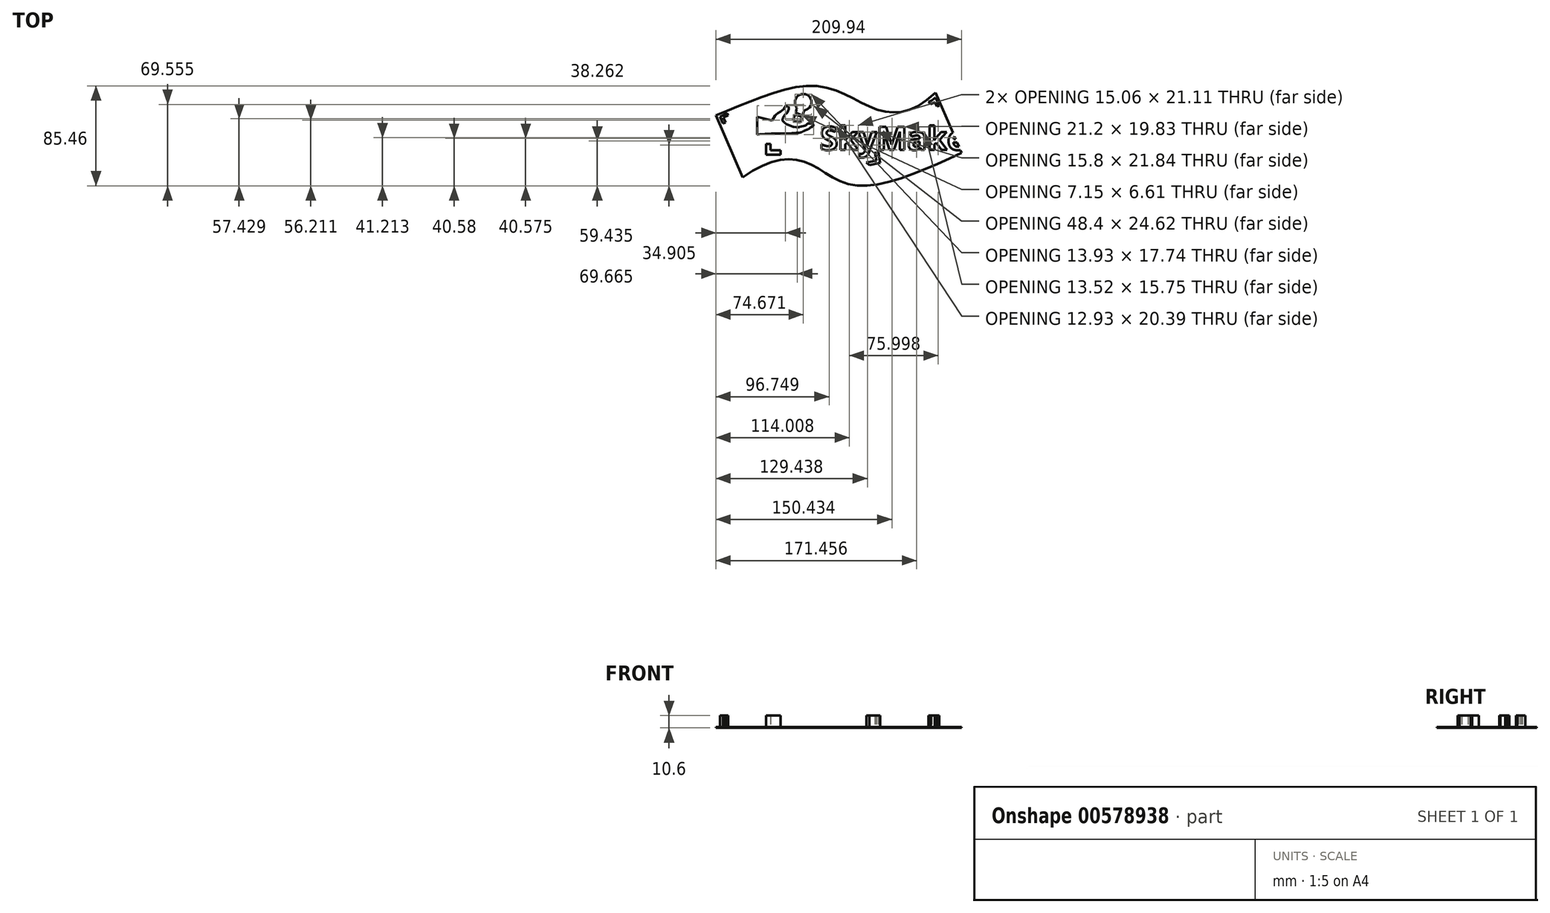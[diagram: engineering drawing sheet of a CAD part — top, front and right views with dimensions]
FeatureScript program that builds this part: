
annotation { "Feature Type Name" : "Feature", "Feature Type Description" : "" }
export const myFeature = defineFeature(function(context is Context, id is Id, definition is map)
    precondition{}
    {
        {
            var Q0;
            Q0=qCreatedBy(makeId("Top.planeOp"),FACE);
            var sketch = newSketch(context, id + "F0", { "sketchPlane" : qUnion([Q0])});
            skLineSegment(sketch, "E0.left", {"start": v(-41.02, -28.62) * mm, "end": v(-63.9, 24.41) * mm});
            skLineSegment(sketch, "E0.right", {"start": v(146.04, -7.8) * mm, "end": v(123.74, 43.89) * mm});
            skFitSpline(sketch, "E1", {"points": [v(-41.02, -28.62) * mm, v(12.17, -15.38) * mm, v(53.5, -35.29) * mm, v(146.04, -7.8) * mm], "startDerivative": vector(200.09, 142.74) * mm, "endDerivative": vector(235.03, 108.17) * mm});
            skFitSpline(sketch, "E2", {"points": [v(123.74, 43.89) * mm, v(75.61, 28.75) * mm, v(22.77, 49.35) * mm, v(-63.9, 24.41) * mm], "startDerivative": vector(-176.83, -170.43) * mm, "endDerivative": vector(-218, -84.69) * mm});
            skSolve(sketch);
        }
        {
            var Q0;
            Q0=qSketchRegion(id+"F0",true);
            extrude(context, id + "F1", {"entities" : qUnion([Q0]), "depth" : 0.6 * mm, "offsetDistance" : 25 * mm});
        }
        {
            var Q0;
            Q0=makeQuery(id+"F1.opExtrude","CAP_FACE",FACE,{"disambiguationData":[OSD([sQuery(id+"F0.wireOp",EDGE,"E0.left"),sQuery(id+"F0.wireOp",EDGE,"E0.right"),sQuery(id+"F0.wireOp",EDGE,"E1"),sQuery(id+"F0.wireOp",EDGE,"E2")])],"isStart":false});
            var sketch = newSketch(context, id + "F2", { "sketchPlane" : qUnion([Q0])});
            skLineSegment(sketch, "E3", {"start": v(-57.77, 17.46) * mm, "end": v(-60.47, 23.24) * mm});
            skLineSegment(sketch, "E4", {"start": v(-60.47, 23.24) * mm, "end": v(-54.23, 26.16) * mm});
            skLineSegment(sketch, "E5", {"start": v(-54.23, 26.16) * mm, "end": v(-53.41, 24.41) * mm});
            skLineSegment(sketch, "E6", {"start": v(-53.41, 24.41) * mm, "end": v(-57.6, 22.46) * mm});
            skLineSegment(sketch, "E7", {"start": v(-57.6, 22.46) * mm, "end": v(-55.72, 18.45) * mm});
            skLineSegment(sketch, "E8", {"start": v(-55.72, 18.45) * mm, "end": v(-57.77, 17.46) * mm});
            skLineSegment(sketch, "E9", {"start": v(120.7, 37.13) * mm, "end": v(123.74, 39.7) * mm});
            skLineSegment(sketch, "E10", {"start": v(123.74, 39.7) * mm, "end": v(126.87, 32.76) * mm});
            skLineSegment(sketch, "E11", {"start": v(126.87, 32.76) * mm, "end": v(124.93, 31.88) * mm});
            skLineSegment(sketch, "E12", {"start": v(124.93, 31.88) * mm, "end": v(123.23, 35.66) * mm});
            skLineSegment(sketch, "E13", {"start": v(123.23, 35.66) * mm, "end": v(119.62, 34.03) * mm});
            skLineSegment(sketch, "E14", {"start": v(119.62, 34.03) * mm, "end": v(117.61, 35.97) * mm});
            skLineSegment(sketch, "E15", {"start": v(117.61, 35.97) * mm, "end": v(120.7, 37.13) * mm});
            skLineSegment(sketch, "E16", {"start": v(67.21, -18.03) * mm, "end": v(76.47, -16.36) * mm});
            skLineSegment(sketch, "E17", {"start": v(76.47, -16.36) * mm, "end": v(74.78, -7.01) * mm});
            skLineSegment(sketch, "E18", {"start": v(74.78, -7.01) * mm, "end": v(71.93, -7.53) * mm});
            skLineSegment(sketch, "E19", {"start": v(71.93, -7.53) * mm, "end": v(73.18, -14.44) * mm});
            skLineSegment(sketch, "E20", {"start": v(73.18, -14.44) * mm, "end": v(64.63, -15.99) * mm});
            skLineSegment(sketch, "E21", {"start": v(64.63, -15.99) * mm, "end": v(67.21, -18.03) * mm});
            skLineSegment(sketch, "E22", {"start": v(-20.87, -2.86) * mm, "end": v(-20.87, -9.16) * mm});
            skLineSegment(sketch, "E23", {"start": v(-20.87, -9.16) * mm, "end": v(-8.52, -9.16) * mm});
            skLineSegment(sketch, "E24", {"start": v(-8.52, -9.16) * mm, "end": v(-8.52, -5.56) * mm});
            skLineSegment(sketch, "E25", {"start": v(-8.52, -5.56) * mm, "end": v(-17.27, -5.56) * mm});
            skLineSegment(sketch, "E26", {"start": v(-17.27, -5.56) * mm, "end": v(-17.27, 0) * mm});
            skLineSegment(sketch, "E27", {"start": v(-17.27, 0) * mm, "end": v(-20.87, 0) * mm});
            skLineSegment(sketch, "E28", {"start": v(-20.87, 0) * mm, "end": v(-20.87, -2.86) * mm});
            skSolve(sketch);
        }
        {
            var Q0;
            Q0 = qSketchRegion(id + "F2", true);
            extrude(context, id + "F3", {"entities" : qUnion([Q0]), "operationType" : NewBodyOperationType.ADD, "depth" : 10 * mm, "offsetDistance" : 25 * mm});
        }
        {
            var Q0;
            Q0=qCreatedBy(makeId("Top.planeOp"),FACE);
            var sketch = newSketch(context, id + "F4", { "sketchPlane" : qUnion([Q0])});
            skLineSegment(sketch, "E29", {"start": v(-28.66, 23.04) * mm, "end": v(-28.66, 8.04) * mm});
            skLineSegment(sketch, "E30", {"start": v(-28.66, 8.04) * mm, "end": v(-26.69, 8.18) * mm});
            skLineSegment(sketch, "E31", {"start": v(-26.69, 8.18) * mm, "end": v(-22.05, 8.48) * mm});
            skLineSegment(sketch, "E32", {"start": v(-22.05, 8.48) * mm, "end": v(-16.7, 8.77) * mm});
            skLineSegment(sketch, "E33", {"start": v(-16.7, 8.77) * mm, "end": v(-13.54, 8.9) * mm});
            skLineSegment(sketch, "E34", {"start": v(-13.54, 8.9) * mm, "end": v(-12.59, 8.9) * mm});
            skLineSegment(sketch, "E35", {"start": v(-12.59, 8.9) * mm, "end": v(-12.08, 8.9) * mm});
            skLineSegment(sketch, "E36", {"start": v(-12.08, 8.9) * mm, "end": v(-10.54, 8.86) * mm});
            skLineSegment(sketch, "E37", {"start": v(-10.54, 8.86) * mm, "end": v(-7.72, 8.8) * mm});
            skLineSegment(sketch, "E38", {"start": v(-7.72, 8.8) * mm, "end": v(-5.06, 8.76) * mm});
            skLineSegment(sketch, "E39", {"start": v(-5.06, 8.76) * mm, "end": v(-3.7, 8.74) * mm});
            skLineSegment(sketch, "E40", {"start": v(-3.7, 8.74) * mm, "end": v(-3.44, 8.75) * mm});
            skLineSegment(sketch, "E41", {"start": v(-3.44, 8.75) * mm, "end": v(-3.15, 8.76) * mm});
            skLineSegment(sketch, "E42", {"start": v(-3.15, 8.76) * mm, "end": v(-1.15, 8.92) * mm});
            skLineSegment(sketch, "E43", {"start": v(-1.15, 8.92) * mm, "end": v(0.81, 9.1) * mm});
            skLineSegment(sketch, "E44", {"start": v(0.81, 9.1) * mm, "end": v(1.1, 9.11) * mm});
            skLineSegment(sketch, "E45", {"start": v(1.1, 9.11) * mm, "end": v(1.39, 9.14) * mm});
            skLineSegment(sketch, "E46", {"start": v(1.39, 9.14) * mm, "end": v(2.76, 9.2) * mm});
            skLineSegment(sketch, "E47", {"start": v(2.76, 9.2) * mm, "end": v(4.3, 9.3) * mm});
            skLineSegment(sketch, "E48", {"start": v(4.3, 9.3) * mm, "end": v(4.68, 9.32) * mm});
            skLineSegment(sketch, "E49", {"start": v(4.68, 9.32) * mm, "end": v(5.17, 9.36) * mm});
            skLineSegment(sketch, "E50", {"start": v(5.17, 9.36) * mm, "end": v(7.1, 9.44) * mm});
            skLineSegment(sketch, "E51", {"start": v(7.1, 9.44) * mm, "end": v(8.6, 9.68) * mm});
            skLineSegment(sketch, "E52", {"start": v(8.6, 9.68) * mm, "end": v(8.88, 9.8) * mm});
            skLineSegment(sketch, "E53", {"start": v(8.88, 9.8) * mm, "end": v(9.07, 9.88) * mm});
            skLineSegment(sketch, "E54", {"start": v(9.07, 9.88) * mm, "end": v(10.04, 10.4) * mm});
            skLineSegment(sketch, "E55", {"start": v(10.04, 10.4) * mm, "end": v(11.2, 11.04) * mm});
            skLineSegment(sketch, "E56", {"start": v(11.2, 11.04) * mm, "end": v(11.5, 11.16) * mm});
            skLineSegment(sketch, "E57", {"start": v(11.5, 11.16) * mm, "end": v(11.9, 11.35) * mm});
            skLineSegment(sketch, "E58", {"start": v(11.9, 11.35) * mm, "end": v(13.49, 11.95) * mm});
            skLineSegment(sketch, "E59", {"start": v(13.49, 11.95) * mm, "end": v(14.57, 12.32) * mm});
            skLineSegment(sketch, "E60", {"start": v(14.57, 12.32) * mm, "end": v(14.73, 12.4) * mm});
            skLineSegment(sketch, "E61", {"start": v(14.73, 12.4) * mm, "end": v(14.89, 12.47) * mm});
            skLineSegment(sketch, "E62", {"start": v(14.89, 12.47) * mm, "end": v(15.73, 13.08) * mm});
            skLineSegment(sketch, "E63", {"start": v(15.73, 13.08) * mm, "end": v(16.82, 13.92) * mm});
            skLineSegment(sketch, "E64", {"start": v(16.82, 13.92) * mm, "end": v(17.1, 14.1) * mm});
            skLineSegment(sketch, "E65", {"start": v(17.1, 14.1) * mm, "end": v(17.38, 14.29) * mm});
            skLineSegment(sketch, "E66", {"start": v(17.38, 14.29) * mm, "end": v(18.87, 15.17) * mm});
            skLineSegment(sketch, "E67", {"start": v(18.87, 15.17) * mm, "end": v(19.73, 15.89) * mm});
            skLineSegment(sketch, "E68", {"start": v(19.73, 15.89) * mm, "end": v(19.7, 16) * mm});
            skLineSegment(sketch, "E69", {"start": v(19.7, 16) * mm, "end": v(19.6, 16.27) * mm});
            skLineSegment(sketch, "E70", {"start": v(19.6, 16.27) * mm, "end": v(18.98, 17) * mm});
            skLineSegment(sketch, "E71", {"start": v(18.98, 17) * mm, "end": v(17.88, 17.45) * mm});
            skLineSegment(sketch, "E72", {"start": v(17.88, 17.45) * mm, "end": v(16.54, 17.51) * mm});
            skLineSegment(sketch, "E73", {"start": v(16.54, 17.51) * mm, "end": v(15.5, 17.4) * mm});
            skLineSegment(sketch, "E74", {"start": v(15.5, 17.4) * mm, "end": v(15.17, 17.32) * mm});
            skLineSegment(sketch, "E75", {"start": v(15.17, 17.32) * mm, "end": v(14.95, 17.28) * mm});
            skLineSegment(sketch, "E76", {"start": v(14.95, 17.28) * mm, "end": v(14.35, 16.98) * mm});
            skLineSegment(sketch, "E77", {"start": v(14.35, 16.98) * mm, "end": v(13.49, 16.42) * mm});
            skLineSegment(sketch, "E78", {"start": v(13.49, 16.42) * mm, "end": v(12.81, 15.89) * mm});
            skLineSegment(sketch, "E79", {"start": v(12.81, 15.89) * mm, "end": v(12.54, 15.65) * mm});
            skLineSegment(sketch, "E80", {"start": v(12.54, 15.65) * mm, "end": v(12.1, 15.58) * mm});
            skLineSegment(sketch, "E81", {"start": v(12.1, 15.58) * mm, "end": v(7.93, 14.49) * mm});
            skLineSegment(sketch, "E82", {"start": v(7.93, 14.49) * mm, "end": v(7.52, 14.34) * mm});
            skLineSegment(sketch, "E83", {"start": v(7.52, 14.34) * mm, "end": v(6.99, 14.3) * mm});
            skLineSegment(sketch, "E84", {"start": v(6.99, 14.3) * mm, "end": v(4.55, 14.36) * mm});
            skLineSegment(sketch, "E85", {"start": v(4.55, 14.36) * mm, "end": v(2.73, 14.44) * mm});
            skLineSegment(sketch, "E86", {"start": v(2.73, 14.44) * mm, "end": v(2.51, 14.41) * mm});
            skLineSegment(sketch, "E87", {"start": v(2.51, 14.41) * mm, "end": v(2.05, 14.63) * mm});
            skLineSegment(sketch, "E88", {"start": v(2.05, 14.63) * mm, "end": v(-2.75, 16.4) * mm});
            skLineSegment(sketch, "E89", {"start": v(-2.75, 16.4) * mm, "end": v(-3.25, 16.53) * mm});
            skLineSegment(sketch, "E90", {"start": v(-3.25, 16.53) * mm, "end": v(-3.43, 16.65) * mm});
            skLineSegment(sketch, "E91", {"start": v(-3.43, 16.65) * mm, "end": v(-5.04, 18.1) * mm});
            skLineSegment(sketch, "E92", {"start": v(-5.04, 18.1) * mm, "end": v(-5.18, 18.26) * mm});
            skLineSegment(sketch, "E93", {"start": v(-5.18, 18.26) * mm, "end": v(-5.3, 18.41) * mm});
            skLineSegment(sketch, "E94", {"start": v(-5.3, 18.41) * mm, "end": v(-6.8, 19.73) * mm});
            skLineSegment(sketch, "E95", {"start": v(-6.8, 19.73) * mm, "end": v(-6.97, 19.83) * mm});
            skLineSegment(sketch, "E96", {"start": v(-6.97, 19.83) * mm, "end": v(-6.83, 22.27) * mm});
            skLineSegment(sketch, "E97", {"start": v(-6.83, 22.27) * mm, "end": v(-4.98, 24.92) * mm});
            skLineSegment(sketch, "E98", {"start": v(-4.98, 24.92) * mm, "end": v(-4.78, 25.05) * mm});
            skLineSegment(sketch, "E99", {"start": v(-4.78, 25.05) * mm, "end": v(-3, 26.61) * mm});
            skLineSegment(sketch, "E100", {"start": v(-3, 26.61) * mm, "end": v(-2.85, 26.8) * mm});
            skLineSegment(sketch, "E101", {"start": v(-2.85, 26.8) * mm, "end": v(-2.66, 27.1) * mm});
            skLineSegment(sketch, "E102", {"start": v(-2.66, 27.1) * mm, "end": v(-2.21, 28.07) * mm});
            skLineSegment(sketch, "E103", {"start": v(-2.21, 28.07) * mm, "end": v(-1.8, 29.53) * mm});
            skLineSegment(sketch, "E104", {"start": v(-1.8, 29.53) * mm, "end": v(-1.77, 30.9) * mm});
            skLineSegment(sketch, "E105", {"start": v(-1.77, 30.9) * mm, "end": v(-2.12, 31.77) * mm});
            skLineSegment(sketch, "E106", {"start": v(-2.12, 31.77) * mm, "end": v(-2.32, 31.95) * mm});
            skLineSegment(sketch, "E107", {"start": v(-2.32, 31.95) * mm, "end": v(-2.6, 32.2) * mm});
            skLineSegment(sketch, "E108", {"start": v(-2.6, 32.2) * mm, "end": v(-3.64, 32.66) * mm});
            skLineSegment(sketch, "E109", {"start": v(-3.64, 32.66) * mm, "end": v(-4.03, 32.57) * mm});
            skLineSegment(sketch, "E110", {"start": v(-4.03, 32.57) * mm, "end": v(-4.16, 32.32) * mm});
            skLineSegment(sketch, "E111", {"start": v(-4.16, 32.32) * mm, "end": v(-5.69, 29.95) * mm});
            skLineSegment(sketch, "E112", {"start": v(-5.69, 29.95) * mm, "end": v(-5.87, 29.73) * mm});
            skLineSegment(sketch, "E113", {"start": v(-5.87, 29.73) * mm, "end": v(-6.12, 29.45) * mm});
            skLineSegment(sketch, "E114", {"start": v(-6.12, 29.45) * mm, "end": v(-7.04, 28.8) * mm});
            skLineSegment(sketch, "E115", {"start": v(-7.04, 28.8) * mm, "end": v(-8.78, 27.71) * mm});
            skLineSegment(sketch, "E116", {"start": v(-8.78, 27.71) * mm, "end": v(-10.84, 26.32) * mm});
            skLineSegment(sketch, "E117", {"start": v(-10.84, 26.32) * mm, "end": v(-12.47, 24.98) * mm});
            skLineSegment(sketch, "E118", {"start": v(-12.47, 24.98) * mm, "end": v(-12.96, 24.47) * mm});
            skLineSegment(sketch, "E119", {"start": v(-12.96, 24.47) * mm, "end": v(-13.28, 24.14) * mm});
            skLineSegment(sketch, "E120", {"start": v(-13.28, 24.14) * mm, "end": v(-15.74, 20.26) * mm});
            skLineSegment(sketch, "E121", {"start": v(-15.74, 20.26) * mm, "end": v(-15.9, 19.83) * mm});
            skLineSegment(sketch, "E122", {"start": v(-15.9, 19.83) * mm, "end": v(-28.66, 23.04) * mm});
            skLineSegment(sketch, "E123", {"start": v(9.34, 22.49) * mm, "end": v(8.04, 18.68) * mm});
            skLineSegment(sketch, "E124", {"start": v(8.04, 18.68) * mm, "end": v(7.12, 18.26) * mm});
            skLineSegment(sketch, "E125", {"start": v(7.12, 18.26) * mm, "end": v(2.8, 19.75) * mm});
            skLineSegment(sketch, "E126", {"start": v(2.8, 19.75) * mm, "end": v(2.2, 20.6) * mm});
            skLineSegment(sketch, "E127", {"start": v(2.2, 20.6) * mm, "end": v(3.48, 24.4) * mm});
            skLineSegment(sketch, "E128", {"start": v(3.48, 24.4) * mm, "end": v(4.45, 24.87) * mm});
            skLineSegment(sketch, "E129", {"start": v(4.45, 24.87) * mm, "end": v(8.82, 23.38) * mm});
            skLineSegment(sketch, "E130", {"start": v(8.82, 23.38) * mm, "end": v(9.34, 22.49) * mm});
            skLineSegment(sketch, "E131", {"start": v(14.49, 29.75) * mm, "end": v(14.9, 30.01) * mm});
            skLineSegment(sketch, "E132", {"start": v(14.9, 30.01) * mm, "end": v(15.99, 31.05) * mm});
            skLineSegment(sketch, "E133", {"start": v(15.99, 31.05) * mm, "end": v(17.05, 32.68) * mm});
            skLineSegment(sketch, "E134", {"start": v(17.05, 32.68) * mm, "end": v(17.63, 34.54) * mm});
            skLineSegment(sketch, "E135", {"start": v(17.63, 34.54) * mm, "end": v(17.73, 36.04) * mm});
            skLineSegment(sketch, "E136", {"start": v(17.73, 36.04) * mm, "end": v(17.68, 36.53) * mm});
            skLineSegment(sketch, "E137", {"start": v(17.68, 36.53) * mm, "end": v(17.61, 37.01) * mm});
            skLineSegment(sketch, "E138", {"start": v(17.61, 37.01) * mm, "end": v(17.16, 38.45) * mm});
            skLineSegment(sketch, "E139", {"start": v(17.16, 38.45) * mm, "end": v(16.15, 40.11) * mm});
            skLineSegment(sketch, "E140", {"start": v(16.15, 40.11) * mm, "end": v(14.73, 41.45) * mm});
            skLineSegment(sketch, "E141", {"start": v(14.73, 41.45) * mm, "end": v(13.42, 42.19) * mm});
            skLineSegment(sketch, "E142", {"start": v(13.42, 42.19) * mm, "end": v(12.96, 42.34) * mm});
            skLineSegment(sketch, "E143", {"start": v(12.96, 42.34) * mm, "end": v(12.32, 42.56) * mm});
            skLineSegment(sketch, "E144", {"start": v(12.32, 42.56) * mm, "end": v(9.07, 42.54) * mm});
            skLineSegment(sketch, "E145", {"start": v(9.07, 42.54) * mm, "end": v(6.14, 41.1) * mm});
            skLineSegment(sketch, "E146", {"start": v(6.14, 41.1) * mm, "end": v(5.67, 40.62) * mm});
            skLineSegment(sketch, "E147", {"start": v(5.67, 40.62) * mm, "end": v(5.2, 40.15) * mm});
            skLineSegment(sketch, "E148", {"start": v(5.2, 40.15) * mm, "end": v(3.8, 37.2) * mm});
            skLineSegment(sketch, "E149", {"start": v(3.8, 37.2) * mm, "end": v(3.82, 33.95) * mm});
            skLineSegment(sketch, "E150", {"start": v(3.82, 33.95) * mm, "end": v(4.05, 33.31) * mm});
            skLineSegment(sketch, "E151", {"start": v(4.05, 33.31) * mm, "end": v(4.13, 33.06) * mm});
            skLineSegment(sketch, "E152", {"start": v(4.13, 33.06) * mm, "end": v(4.26, 32.74) * mm});
            skLineSegment(sketch, "E153", {"start": v(4.26, 32.74) * mm, "end": v(4.97, 31.2) * mm});
            skLineSegment(sketch, "E154", {"start": v(4.97, 31.2) * mm, "end": v(5.2, 29.7) * mm});
            skLineSegment(sketch, "E155", {"start": v(5.2, 29.7) * mm, "end": v(5.1, 29.37) * mm});
            skLineSegment(sketch, "E156", {"start": v(5.1, 29.37) * mm, "end": v(4.36, 27.16) * mm});
            skLineSegment(sketch, "E157", {"start": v(4.36, 27.16) * mm, "end": v(4.97, 26.3) * mm});
            skLineSegment(sketch, "E158", {"start": v(4.97, 26.3) * mm, "end": v(9.2, 24.83) * mm});
            skLineSegment(sketch, "E159", {"start": v(9.2, 24.83) * mm, "end": v(10.27, 25.11) * mm});
            skLineSegment(sketch, "E160", {"start": v(10.27, 25.11) * mm, "end": v(11, 27.37) * mm});
            skLineSegment(sketch, "E161", {"start": v(11, 27.37) * mm, "end": v(11.11, 27.7) * mm});
            skLineSegment(sketch, "E162", {"start": v(11.11, 27.7) * mm, "end": v(12.3, 28.7) * mm});
            skLineSegment(sketch, "E163", {"start": v(12.3, 28.7) * mm, "end": v(13.95, 29.45) * mm});
            skLineSegment(sketch, "E164", {"start": v(13.95, 29.45) * mm, "end": v(14.28, 29.65) * mm});
            skLineSegment(sketch, "E165", {"start": v(14.28, 29.65) * mm, "end": v(14.49, 29.75) * mm});
            skSolve(sketch);
        }
        {
            var Q0;
            Q0 = qSketchRegion(id + "F4", true);
            extrude(context, id + "F5", {"entities" : qUnion([Q0]), "operationType" : NewBodyOperationType.REMOVE, "endBound" : BoundingType.SYMMETRIC, "oppositeDirection" : true, "depth" : 30 * mm, "offsetDistance" : 25 * mm});
        }
        {
            var Q0;
            Q0=makeQuery(id+"F1.opExtrude","CAP_FACE",FACE,{"disambiguationData":[OSD([sQuery(id+"F0.wireOp",EDGE,"E0.left"),sQuery(id+"F0.wireOp",EDGE,"E0.right"),sQuery(id+"F0.wireOp",EDGE,"E1"),sQuery(id+"F0.wireOp",EDGE,"E2")])],"isStart":false});
            var sketch = newSketch(context, id + "F6", { "sketchPlane" : qUnion([Q0])});
            skText(sketch, "E166", { "text": "SkyMaker", "fontName": "OpenSans-Bold.ttf"});
            const initialGuessF6  = {"E166": [0.02511, -0.0052, 1, 0, 0.02]};
            skSetInitialGuess(sketch, initialGuessF6);
            skSolve(sketch);
        }
        {
            var Q0;
            Q0 = qSketchRegion(id + "F6", true);
            extrude(context, id + "F7", {"entities" : qUnion([Q0]), "operationType" : NewBodyOperationType.REMOVE, "endBound" : BoundingType.SYMMETRIC, "oppositeDirection" : true, "depth" : 25 * mm, "offsetDistance" : 25 * mm});
        }
    });
